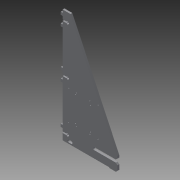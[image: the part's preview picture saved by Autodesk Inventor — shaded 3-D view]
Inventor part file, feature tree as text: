
AUTODESK INVENTOR PART (.ipt)
format: ipt  version: 2015 (Build 190159000, 159)  size: 561,664 bytes
history: native  units: mm
features: extrude x1, sketch x1
ambient origin geometry x8: Origin, YZ Plane, XZ Plane, XY Plane, X Axis, Y Axis, Z Axis, Center Point
bodies: Solid1 (feature_tree)
feature tree (2):
  extrude  "Extrusion1"  [1 undecoded]
  sketch  "Sketch1"  dims[d0=6.0mm d1=0.0mm]
note: 1 required parameter value undecoded (feature->parameter linkage not recoverable at this tier; creation-order binding heuristic only, values carry confidence <= 0.55)
